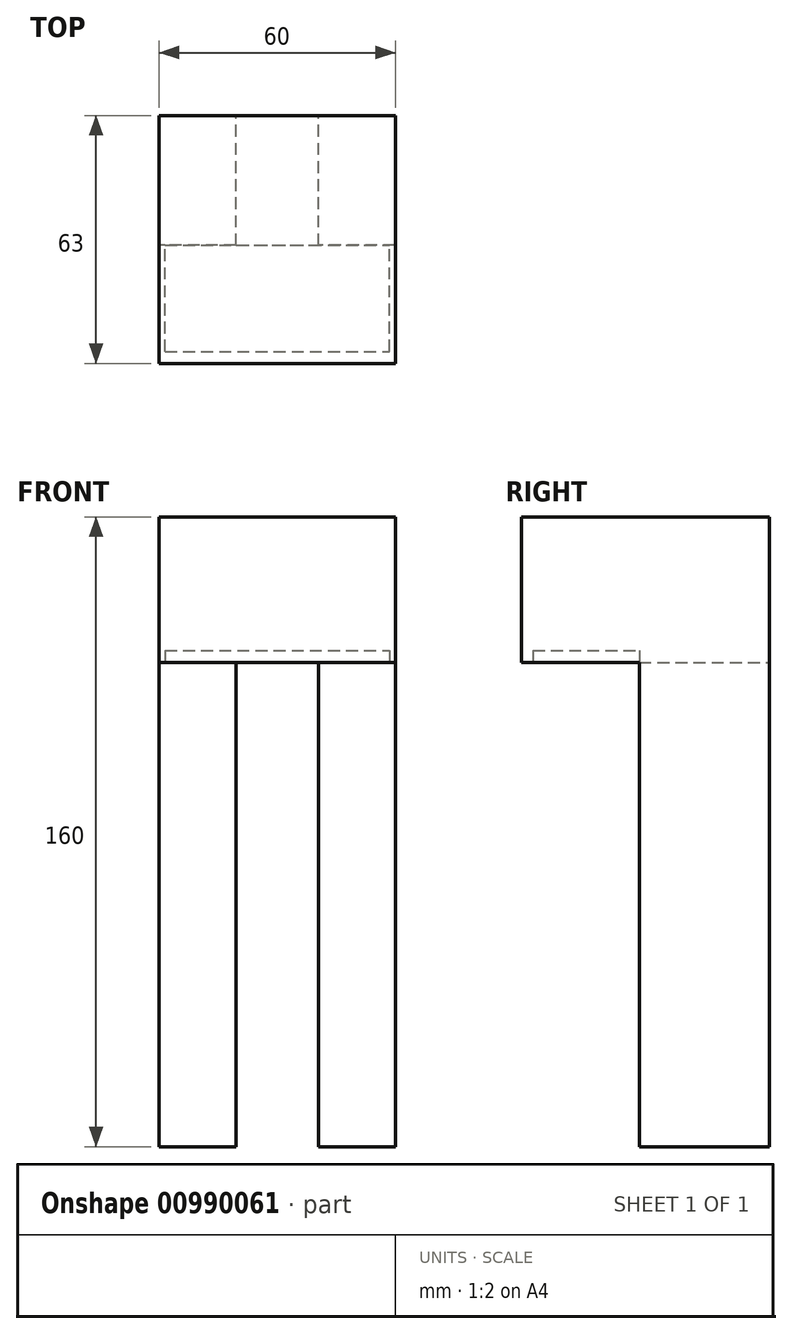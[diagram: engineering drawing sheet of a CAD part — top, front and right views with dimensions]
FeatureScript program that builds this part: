
annotation { "Feature Type Name" : "Feature", "Feature Type Description" : "" }
export const myFeature = defineFeature(function(context is Context, id is Id, definition is map)
    precondition{}
    {
        {
            var Q0;
            Q0=qCreatedBy(makeId("Top.planeOp"),FACE);
            var sketch = newSketch(context, id + "F0", { "sketchPlane" : qUnion([Q0])});
            skLineSegment(sketch, "E0.bottom", {"start": v(30, -16.5) * mm, "end": v(-30, -16.5) * mm});
            skLineSegment(sketch, "E0.top", {"start": v(30, 16.5) * mm, "end": v(-30, 16.5) * mm});
            skLineSegment(sketch, "E0.left", {"start": v(30, -16.5) * mm, "end": v(30, 16.5) * mm});
            skLineSegment(sketch, "E0.right", {"start": v(-30, -16.5) * mm, "end": v(-30, 16.5) * mm});
            skPoint(sketch, "E0.middle", {"position": v(0, 0) * mm});
            skSolve(sketch);
        }
        {
            var Q0;
            Q0 = qSketchRegion(id + "F0", true);
            extrude(context, id + "F1", {"entities" : qUnion([Q0]), "depth" : 160 * mm, "offsetDistance" : 25 * mm});
        }
        {
            var Q0;
            Q0=makeQuery(id+"F1.opExtrude","SWEPT_FACE",FACE,{"disambiguationData":[OSD([sQuery(id+"F0.wireOp",EDGE,"E0.right")])]});
            var sketch = newSketch(context, id + "F2", { "sketchPlane" : qUnion([Q0])});
            skPoint(sketch, "E1", {"position": v(16.5, 123) * mm});
            skLineSegment(sketch, "E2.bottom", {"start": v(16.5, 123) * mm, "end": v(-13.5, 123) * mm});
            skLineSegment(sketch, "E2.top", {"start": v(16.5, 0) * mm, "end": v(-13.5, 0) * mm});
            skLineSegment(sketch, "E2.left", {"start": v(16.5, 123) * mm, "end": v(16.5, 0) * mm});
            skLineSegment(sketch, "E2.right", {"start": v(-13.5, 123) * mm, "end": v(-13.5, 0) * mm});
            skSolve(sketch);
        }
        {
            var Q0;
            Q0=makeQuery(id+"F2.imprint","IMPRINT",FACE,{"disambiguationData":[TD([[makeQuery(id+"F2.imprint","IMPRINT",EDGE,{"derivedFrom":sQuery(id+"F2.wireOp",EDGE,"E2.bottom")}),1.0]])]});
            extrude(context, id + "F3", {"entities" : qUnion([Q0]), "operationType" : NewBodyOperationType.REMOVE, "endBound" : BoundingType.THROUGH_ALL, "oppositeDirection" : true, "depth" : 25 * mm, "offsetDistance" : 25 * mm});
        }
        {
            var Q0;
            Q0=makeQuery(id+"F1.opExtrude","SWEPT_FACE",FACE,{"disambiguationData":[OSD([sQuery(id+"F0.wireOp",EDGE,"E0.top")])]});
            var sketch = newSketch(context, id + "F4", { "sketchPlane" : qUnion([Q0])});
            skLineSegment(sketch, "E3.bottom", {"start": v(-10.5, 123) * mm, "end": v(10.5, 123) * mm});
            skLineSegment(sketch, "E3.top", {"start": v(-10.5, -123) * mm, "end": v(10.5, -123) * mm});
            skLineSegment(sketch, "E3.left", {"start": v(-10.5, 123) * mm, "end": v(-10.5, -123) * mm});
            skLineSegment(sketch, "E3.right", {"start": v(10.5, 123) * mm, "end": v(10.5, -123) * mm});
            skPoint(sketch, "E3.middle", {"position": v(0, 0) * mm});
            skSolve(sketch);
        }
        {
            var Q0;
            {var subQ0=sQuery(id+"F4.wireOp",EDGE,"E3.top");Q0=makeQuery(id+"F4.imprint","IMPRINT",FACE,{"disambiguationData":[TD([[makeQuery(id+"F4.imprint","IMPRINT",EDGE,{"derivedFrom":subQ0}),1.0]])]});}
            var Q1;
            {var subQ0=sQuery(id+"F4.wireOp",EDGE,"E3.bottom");Q1=makeQuery(id+"F4.imprint","IMPRINT",FACE,{"disambiguationData":[TD([[makeQuery(id+"F4.imprint","IMPRINT",EDGE,{"derivedFrom":subQ0}),-1.0]])]});}
            extrude(context, id + "F5", {"entities" : qUnion([Q0, Q1]), "operationType" : NewBodyOperationType.REMOVE, "endBound" : BoundingType.THROUGH_ALL, "oppositeDirection" : true, "depth" : 25 * mm, "offsetDistance" : 25 * mm});
        }
        {
            var Q0;
            Q0=qCreatedBy(makeId("Top.planeOp"),FACE);
            cPlane(context, id + "F6", {"entities" : qUnion([Q0]), "cplaneType" : CPlaneType.OFFSET, "offset" : 123 * mm, "width" : 150 * mm, "height" : 150 * mm});
        }
        {
            var Q0;
            Q0=qCreatedBy(id+"F6.planeOp",FACE);
            var sketch = newSketch(context, id + "F7", { "sketchPlane" : qUnion([Q0])});
            skLineSegment(sketch, "E4.bottom", {"start": v(-28.5, -13.5) * mm, "end": v(28.5, -13.5) * mm});
            skLineSegment(sketch, "E4.top", {"start": v(-28.5, 13.5) * mm, "end": v(28.5, 13.5) * mm});
            skLineSegment(sketch, "E4.left", {"start": v(-28.5, -13.5) * mm, "end": v(-28.5, 13.5) * mm});
            skLineSegment(sketch, "E4.right", {"start": v(28.5, -13.5) * mm, "end": v(28.5, 13.5) * mm});
            skPoint(sketch, "E4.middle", {"position": v(0, 0) * mm});
            skSolve(sketch);
        }
        {
            var Q0;
            Q0 = qSketchRegion(id + "F7", true);
            extrude(context, id + "F8", {"entities" : qUnion([Q0]), "operationType" : NewBodyOperationType.REMOVE, "depth" : 3 * mm, "offsetDistance" : 25 * mm});
        }
        {
            var Q0;
            Q0=makeQuery(id+"F1.opExtrude","SWEPT_FACE",FACE,{"disambiguationData":[OSD([sQuery(id+"F0.wireOp",EDGE,"E0.top")])]});
            var sketch = newSketch(context, id + "F9", { "sketchPlane" : qUnion([Q0])});
            skLineSegment(sketch, "E5.bottom", {"start": v(30, 160) * mm, "end": v(10.5, 160) * mm});
            skLineSegment(sketch, "E5.top", {"start": v(30, 0) * mm, "end": v(10.5, 0) * mm});
            skLineSegment(sketch, "E5.left", {"start": v(30, 160) * mm, "end": v(30, 0) * mm});
            skLineSegment(sketch, "E5.right", {"start": v(10.5, 160) * mm, "end": v(10.5, 0) * mm});
            skLineSegment(sketch, "E6.bottom", {"start": v(-30, 160) * mm, "end": v(-10.5, 160) * mm});
            skLineSegment(sketch, "E6.top", {"start": v(-30, 0) * mm, "end": v(-10.5, 0) * mm});
            skLineSegment(sketch, "E6.left", {"start": v(-30, 160) * mm, "end": v(-30, 0) * mm});
            skLineSegment(sketch, "E6.right", {"start": v(-10.5, 160) * mm, "end": v(-10.5, 0) * mm});
            skLineSegment(sketch, "E7.bottom", {"start": v(10.5, 160) * mm, "end": v(-10.5, 160) * mm});
            skLineSegment(sketch, "E7.top", {"start": v(10.5, 123) * mm, "end": v(-10.5, 123) * mm});
            skLineSegment(sketch, "E7.left", {"start": v(10.5, 160) * mm, "end": v(10.5, 123) * mm});
            skLineSegment(sketch, "E7.right", {"start": v(-10.5, 160) * mm, "end": v(-10.5, 123) * mm});
            skSolve(sketch);
        }
        {
            var Q0;
            Q0 = qSketchRegion(id + "F9", true);
            extrude(context, id + "F10", {"entities" : qUnion([Q0]), "operationType" : NewBodyOperationType.ADD, "depth" : 30 * mm, "offsetDistance" : 25 * mm});
        }
    });
